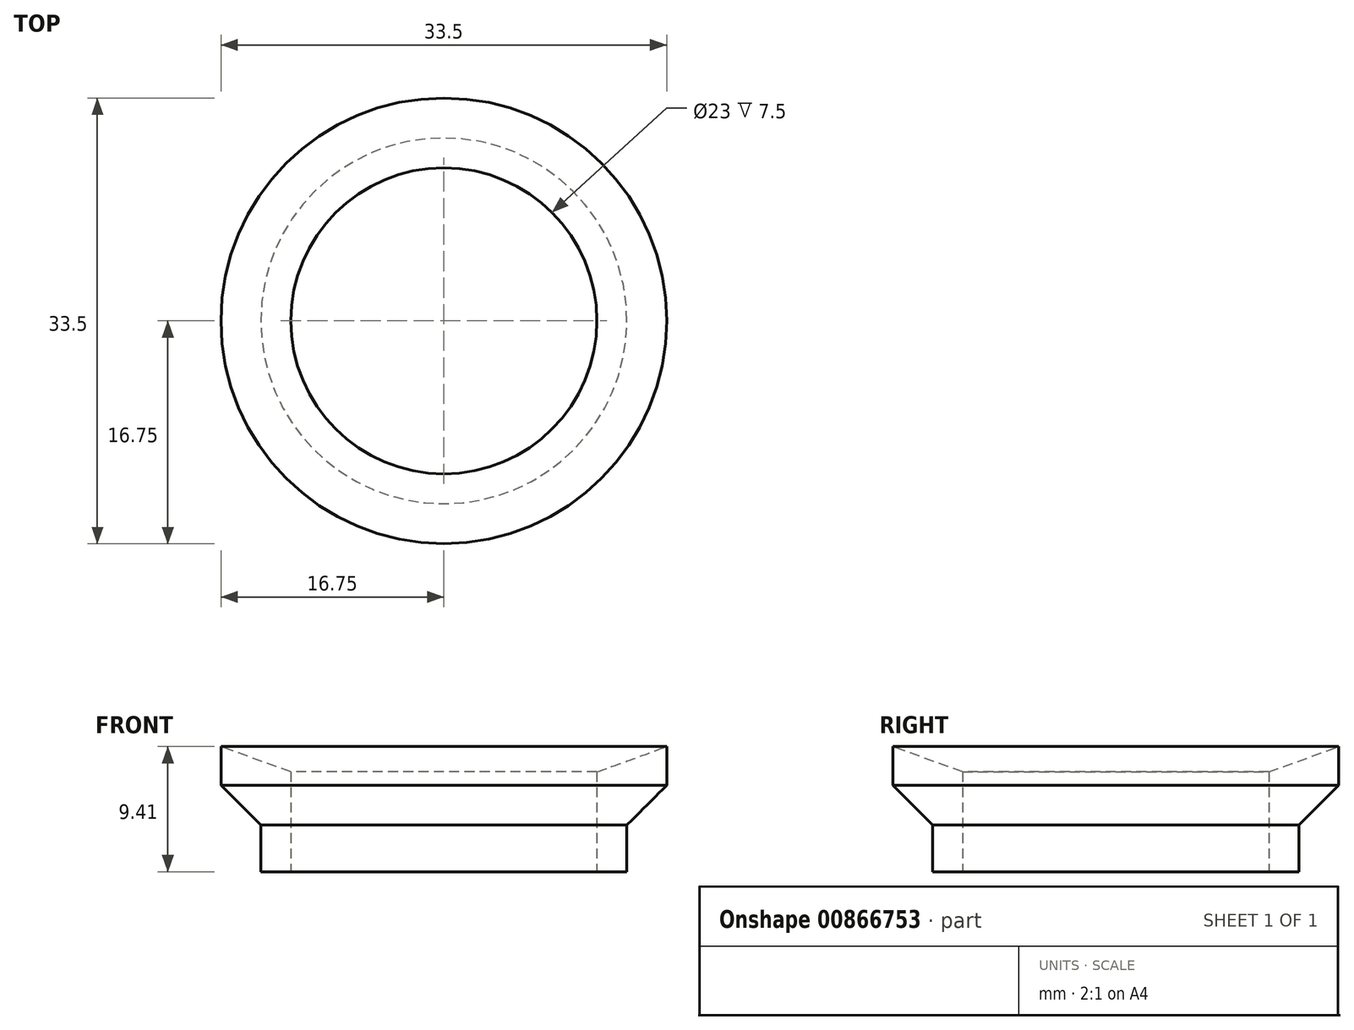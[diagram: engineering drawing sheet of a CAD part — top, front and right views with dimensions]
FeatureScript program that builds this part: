
annotation { "Feature Type Name" : "Feature", "Feature Type Description" : "" }
export const myFeature = defineFeature(function(context is Context, id is Id, definition is map)
    precondition{}
    {
        {
            var Q0;
            Q0=qCreatedBy(makeId("Top.planeOp"),FACE);
            var sketch = newSketch(context, id + "F0", { "sketchPlane" : qUnion([Q0])});
            skCircle(sketch, "E0", {"center": v(0, 0) * mm, "radius": 11.5 * mm});
            skCircle(sketch, "E1", {"center": v(0, 0) * mm, "radius": 13.75 * mm});
            skSolve(sketch);
        }
        {
            var Q0;
            Q0=makeQuery(id+"F0.imprint","IMPRINT",FACE,{"disambiguationData":[TD([[makeQuery(id+"F0.imprint","IMPRINT",EDGE,{"derivedFrom":sQuery(id+"F0.wireOp",EDGE,"E0")}),-1.0]])]});
            extrude(context, id + "F1", {"entities" : qUnion([Q0]), "depth" : 8.4 * mm, "offsetDistance" : 25 * mm});
        }
        {
            var Q0;
            Q0=qCreatedBy(makeId("Top.planeOp"),FACE);
            cPlane(context, id + "F2", {"entities" : qUnion([Q0]), "cplaneType" : CPlaneType.OFFSET, "offset" : 5.5 * mm, "width" : 150 * mm, "height" : 150 * mm});
        }
        {
            var Q0;
            Q0=qCreatedBy(id+"F2.planeOp",FACE);
            var sketch = newSketch(context, id + "F3", { "sketchPlane" : qUnion([Q0])});
            skLineSegment(sketch, "E2.bottom", {"start": v(16.75, -16.75) * mm, "end": v(-16.75, -16.75) * mm});
            skLineSegment(sketch, "E2.top", {"start": v(16.75, 16.75) * mm, "end": v(-16.75, 16.75) * mm});
            skLineSegment(sketch, "E2.left", {"start": v(16.75, -16.75) * mm, "end": v(16.75, 16.75) * mm});
            skLineSegment(sketch, "E2.right", {"start": v(-16.75, -16.75) * mm, "end": v(-16.75, 16.75) * mm});
            skPoint(sketch, "E2.middle", {"position": v(0, 0) * mm});
            skCircle(sketch, "E3", {"center": v(0, 0) * mm, "radius": 11.5 * mm});
            skCircle(sketch, "E4", {"center": v(0, 0) * mm, "radius": 16.75 * mm});
            skSolve(sketch);
        }
        {
            var Q0;
            Q0=makeQuery(id+"F3.imprint","IMPRINT",FACE,{"disambiguationData":[TD([[makeQuery(id+"F3.imprint","IMPRINT",EDGE,{"derivedFrom":sQuery(id+"F3.wireOp",EDGE,"E3")}),-1.0]])]});
            extrude(context, id + "F4", {"entities" : qUnion([Q0]), "operationType" : NewBodyOperationType.ADD, "depth" : 4 * mm, "offsetDistance" : 25 * mm});
        }
        {
            var Q0;
            Q0=makeQuery(id+"F4.opExtrude","CAP_EDGE",EDGE,{"disambiguationData":[OSD([sQuery(id+"F3.wireOp",EDGE,"E3")])],"isStart":false});
            chamfer(context, id + "F5", {"entities" : qUnion([Q0]), "chamferType" : ChamferType.OFFSET_ANGLE, "width" : 2 * mm, "oppositeDirection" : false, "angle" : 70 * degree, "tangentPropagation" : true});
        }
        {
            var Q0;
            Q0=makeQuery(id+"F4.boolean.opBoolean","INTERSECT",EDGE,{"derivedFrom":[makeQuery(id+"F1.opExtrude","SWEPT_FACE",FACE,{"disambiguationData":[OSD([sQuery(id+"F0.wireOp",EDGE,"E1")])]}),makeQuery(id+"F4.opExtrude","CAP_FACE",FACE,{"disambiguationData":[OSD([sQuery(id+"F3.wireOp",EDGE,"E2.bottom"),sQuery(id+"F3.wireOp",EDGE,"E2.top"),sQuery(id+"F3.wireOp",EDGE,"E2.left"),sQuery(id+"F3.wireOp",EDGE,"E2.right"),sQuery(id+"F3.wireOp",EDGE,"E3")])],"isStart":true})]});
            chamfer(context, id + "F6", {"entities" : qUnion([Q0]), "width" : 2 * mm, "tangentPropagation" : true});
        }
        {
            var Q0;
            Q0=makeQuery(id+"F4.opExtrude","CAP_EDGE",EDGE,{"disambiguationData":[OSD([sQuery(id+"F3.wireOp",EDGE,"E4")])],"isStart":true});
            chamfer(context, id + "F7", {"entities" : qUnion([Q0]), "width" : 1 * mm, "tangentPropagation" : true});
        }
    });
